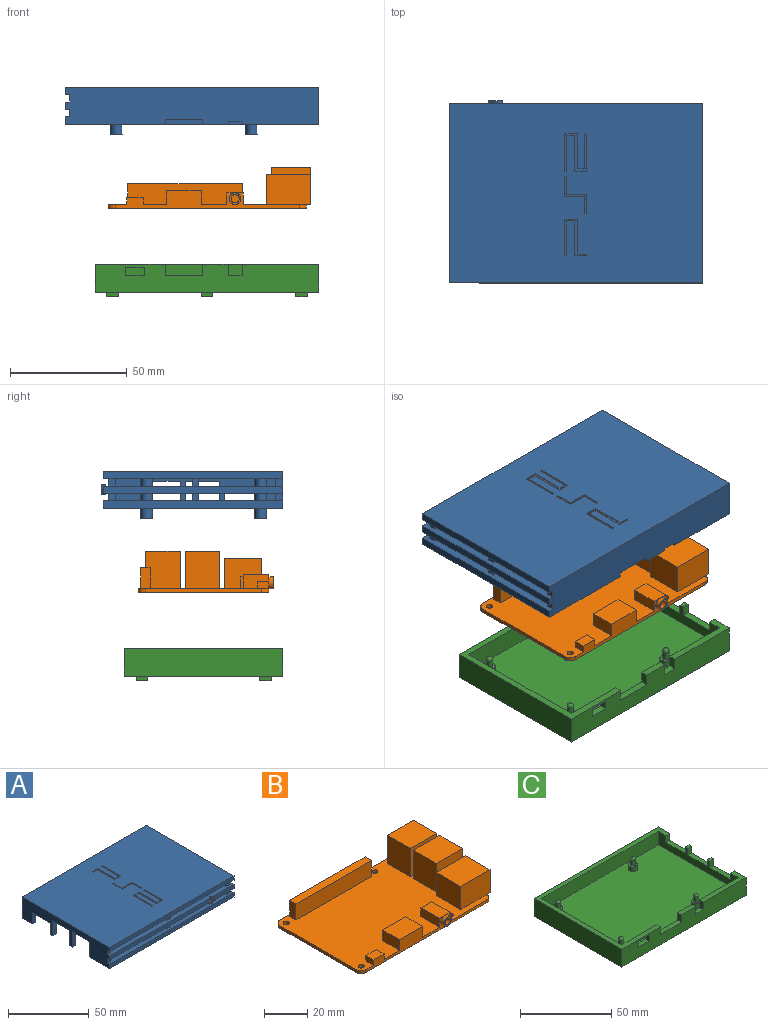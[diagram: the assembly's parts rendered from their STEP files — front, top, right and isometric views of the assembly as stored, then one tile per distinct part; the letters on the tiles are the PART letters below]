
ASSEMBLY  parts=3 mates=2
PART A: 158 faces, bbox 109x78x20.4 mm
  f0: plane 11x3mm, normal (0,0,-1), area 33mm2, adj f2,f3,f152,f156
  f1: plane 33x9mm, normal (0,0,-1), area 117mm2, adj f2,f3,f24,f27,f149,f153
  f2: plane 109x16mm, normal (0,1,0), area 1692mm2, adj f0,f1,f6,f12,f13,f24,f28,f29
  f3: plane 104x13mm, normal (0,-1,0), area 1260mm2, adj f0,f1,f6,f12,f13,f23,f25,f27
  f4: plane 3x2mm, normal (0,0,-1), area 6mm2, adj f24,f27,f146,f150
  f5: plane 3x2mm, normal (0,0,-1), area 6mm2, adj f24,f27,f144,f147
  f6: plane 109x77mm, normal (0,0,-1), area 855.6mm2, adj f2,f3,f7,f8,f9,f12,f14,f19
  f7: plane 19.8x3.21mm, normal (0,-1,0), area 58.7mm2, adj f6,f51,f65,f120,f128,f129,f130,f131
  f8: plane 3.2x3mm, normal (1,0,0), area 9.6mm2, adj f6,f21,f53,f60
  f9: plane 3.2x3mm, normal (1,0,0), area 9.6mm2, adj f6,f53,f61,f62
  f10: plane 3.2x3mm, normal (1,0,0), area 9.6mm2, adj f18,f51,f52,f58
  f11: plane 3.2x3mm, normal (1,0,0), area 9.6mm2, adj f51,f52,f59,f63
  f12: plane 3.2x3mm, normal (1,0,0), area 9.6mm2, adj f2,f3,f6,f53
  f13: plane 3.2x3mm, normal (1,0,0), area 9.6mm2, adj f2,f3,f51,f52
  f14: plane 3.2x3mm, normal (-1,0,0), area 9.6mm2, adj f6,f21,f53,f60
  f15: plane 3.2x3mm, normal (-1,0,0), area 9.6mm2, adj f18,f51,f52,f58
  f16: plane 3.2x3mm, normal (0,-1,0), area 9.6mm2, adj f24,f27,f51,f52
  f17: plane 3.2x3mm, normal (0,-1,0), area 9.6mm2, adj f48,f50,f51,f52
  f18: plane 3.2x3mm, normal (0,-1,0), area 9.6mm2, adj f10,f15,f51,f52
  f19: plane 3.2x3mm, normal (0,-1,0), area 9.6mm2, adj f6,f24,f27,f53
  f20: plane 3.2x3mm, normal (0,-1,0), area 9.6mm2, adj f6,f49,f53,f54
  f21: plane 3.2x3mm, normal (0,-1,0), area 9.6mm2, adj f6,f8,f14,f53
  f22: plane 101x10mm, normal (0,1,0), area 382.8mm2, adj f6,f23,f27,f30,f31,f48,f49,f50
  f23: plane 101x69mm, normal (0,0,-1), area 6890.5mm2, adj f3,f22,f27,f30,f32,f36,f41,f44
  f24: plane 77x16mm, normal (-1,0,0), area 733.6mm2, adj f1,f2,f4,f5,f6,f16,f19,f28
  f25: plane 62x3mm, normal (-1,0,0), area 186mm2, adj f3,f26,f28,f31
  f26: plane 90x3mm, normal (0,1,0), area 270mm2, adj f25,f27,f28,f31
  f27: plane 72x13mm, normal (1,0,0), area 409.6mm2, adj f1,f3,f4,f5,f6,f16,f19,f22
  f28: plane 109x77mm, normal (0,0,-1), area 2393.6mm2, adj f2,f3,f24,f25,f26,f27,f56,f66
  f29: plane 109x77mm, normal (0,0,1), area 8284.7mm2, adj f2,f24,f55,f64,f84,f85,f86,f87
  f30: plane 69x10mm, normal (-1,0,0), area 267.6mm2, adj f3,f6,f22,f23,f31,f51,f52,f53
  f31: plane 101x69mm, normal (0,0,1), area 1335.6mm2, adj f3,f22,f25,f26,f27,f30,f67,f68
  f32: cylinder r=2.5mm len=17.4mm, axis (0,0,1), area 273.3mm2, adj f23,f34
  f33: cylinder r=1.38mm len=17.4mm, axis (0,0,1), area 150.3mm2, adj f34,f35
  f34: plane 5x5mm, normal (0,0,-1), area 13.7mm2, adj f32,f33
  f35: plane 2.75x2.75mm, normal (0,0,-1), area 5.9mm2, adj f33
  f36: cylinder r=2.5mm len=17.4mm, axis (0,0,1), area 273.3mm2, adj f23,f38
  f37: cylinder r=1.38mm len=17.4mm, axis (0,0,1), area 150.3mm2, adj f38,f39
  f38: plane 5x5mm, normal (0,0,-1), area 13.7mm2, adj f36,f37
  f39: plane 2.75x2.75mm, normal (0,0,-1), area 5.9mm2, adj f37
  f40: cylinder r=1.38mm len=17.4mm, axis (0,0,1), area 150.3mm2, adj f42,f43
  f41: cylinder r=2.5mm len=17.4mm, axis (0,0,1), area 273.3mm2, adj f23,f42
  f42: plane 5x5mm, normal (0,0,-1), area 13.7mm2, adj f40,f41
  f43: plane 2.75x2.75mm, normal (0,0,-1), area 5.9mm2, adj f40
  f44: cylinder r=2.5mm len=17.4mm, axis (0,0,1), area 273.3mm2, adj f23,f46
  f45: cylinder r=1.38mm len=17.4mm, axis (0,0,1), area 150.3mm2, adj f46,f47
  f46: plane 5x5mm, normal (0,0,-1), area 13.7mm2, adj f44,f45
  f47: plane 2.75x2.75mm, normal (0,0,-1), area 5.9mm2, adj f45
  f48: plane 3.2x3mm, normal (-1,0,0), area 9.6mm2, adj f17,f22,f51,f52
  f49: plane 3.2x3mm, normal (1,0,0), area 9.6mm2, adj f6,f20,f22,f53
  f50: plane 3.2x3mm, normal (1,0,0), area 9.6mm2, adj f17,f22,f51,f52
  f51: plane 109x77mm, normal (0,0,1), area 858.2mm2, adj f2,f3,f7,f10,f11,f13,f15,f16
  f52: plane 109x77mm, normal (0,0,-1), area 860mm2, adj f2,f3,f10,f11,f13,f15,f16,f17
  f53: plane 109x77mm, normal (0,0,1), area 860mm2, adj f2,f3,f8,f9,f12,f14,f19,f20
  f54: plane 3.2x3mm, normal (-1,0,0), area 9.6mm2, adj f6,f20,f22,f53
  f55: plane 109x3.2mm, normal (0,-1,0), area 348.8mm2, adj f24,f29,f52,f64
  f56: plane 109x3.2mm, normal (0,-1,0), area 348.8mm2, adj f24,f28,f53,f66
  f57: plane 88.35x3.24mm, normal (0,-1,0), area 280.6mm2, adj f6,f24,f51,f119,f125
  f58: plane 3.2x3mm, normal (0,1,0), area 9.6mm2, adj f10,f15,f51,f52
  f59: plane 3.2x3mm, normal (0,-1,0), area 9.6mm2, adj f11,f30,f51,f52
  f60: plane 3.2x3mm, normal (0,1,0), area 9.6mm2, adj f6,f8,f14,f53
  f61: plane 3.2x3mm, normal (0,-1,0), area 9.6mm2, adj f6,f9,f30,f53
  f62: plane 3.2x3mm, normal (0,1,0), area 9.6mm2, adj f6,f9,f30,f53
  f63: plane 3.2x3mm, normal (0,1,0), area 9.6mm2, adj f11,f30,f51,f52
  f64: plane 77x3.2mm, normal (1,0,0), area 246.4mm2, adj f2,f29,f52,f55
  f65: plane 77x3.2mm, normal (1,0,0), area 246.4mm2, adj f2,f6,f7,f51
  f66: plane 77x3.2mm, normal (1,0,0), area 246.4mm2, adj f2,f28,f53,f56
  f67: cylinder r=1mm len=3mm, axis (0,0,-1), area 18.8mm2, adj f28,f31
  f68: cylinder r=1mm len=3mm, axis (0,0,-1), area 18.8mm2, adj f28,f31
  f69: cylinder r=1mm len=3mm, axis (0,0,-1), area 18.8mm2, adj f28,f31
  f70: cylinder r=1mm len=3mm, axis (0,0,-1), area 18.8mm2, adj f28,f31
  f71: cylinder r=1mm len=3mm, axis (0,0,-1), area 18.8mm2, adj f28,f31
  f72: cylinder r=1mm len=3mm, axis (0,0,-1), area 18.8mm2, adj f28,f31
  f73: cylinder r=1mm len=3mm, axis (0,0,-1), area 18.8mm2, adj f28,f31
  f74: cylinder r=1mm len=3mm, axis (0,0,-1), area 18.8mm2, adj f28,f31
  f75: cylinder r=1mm len=3mm, axis (0,0,-1), area 18.8mm2, adj f28,f31
  f76: cylinder r=1mm len=3mm, axis (0,0,-1), area 18.8mm2, adj f28,f31
  f77: cylinder r=1mm len=3mm, axis (0,0,-1), area 18.8mm2, adj f28,f31
  f78: cylinder r=1mm len=3mm, axis (0,0,-1), area 18.8mm2, adj f28,f31
  f79: cylinder r=1mm len=3mm, axis (0,0,-1), area 18.8mm2, adj f28,f31
  f80: cylinder r=1mm len=3mm, axis (0,0,-1), area 18.8mm2, adj f28,f31
  f81: cylinder r=1mm len=3mm, axis (0,0,-1), area 18.8mm2, adj f28,f31
  f82: cylinder r=1mm len=3mm, axis (0,0,-1), area 18.8mm2, adj f28,f31
  f83: cylinder r=1mm len=3mm, axis (0,0,-1), area 18.8mm2, adj f28,f31
  f84: plane 0.8x0.4mm, normal (0,-1,0), area 0.3mm2, adj f29,f85,f95,f96
  f85: plane 15.2x0.4mm, normal (1,0,0), area 6.1mm2, adj f29,f84,f86,f96
  f86: plane 3.4x0.4mm, normal (0,-1,0), area 1.4mm2, adj f29,f85,f87,f96
  f87: plane 15.2x0.4mm, normal (-1,0,0), area 6.1mm2, adj f29,f86,f88,f96
  f88: plane 5.1x0.4mm, normal (0,-1,0), area 2mm2, adj f29,f87,f89,f96
  f89: plane 16x0.4mm, normal (1,0,0), area 6.4mm2, adj f29,f88,f90,f96
  f90: plane 0.8x0.4mm, normal (0,1,0), area 0.3mm2, adj f29,f89,f91,f96
  f91: plane 15x0.4mm, normal (-1,0,0), area 6mm2, adj f29,f90,f92,f96
  f92: plane 3x0.4mm, normal (0,1,0), area 1.2mm2, adj f29,f91,f93,f96
  f93: plane 15x0.4mm, normal (1,0,0), area 6mm2, adj f29,f92,f94,f96
  f94: plane 5.5x0.4mm, normal (0,1,0), area 2.2mm2, adj f29,f93,f95,f96
  f95: plane 16x0.4mm, normal (-1,0,0), area 6.4mm2, adj f29,f84,f94,f96
  f96: plane 16x9.3mm, normal (0,0,1), area 52.1mm2, adj f84,f85,f86,f87,f88,f89,f90,f91
  f97: plane 8.5x0.4mm, normal (0,1,0), area 3.4mm2, adj f29,f98,f104,f105
  f98: plane 7.6x0.4mm, normal (1,0,0), area 3mm2, adj f29,f97,f99,f105
  f99: plane 0.8x0.4mm, normal (0,1,0), area 0.3mm2, adj f29,f98,f100,f105
  f100: plane 8.4x0.4mm, normal (-1,0,0), area 3.4mm2, adj f29,f99,f101,f105
  f101: plane 8.6x0.4mm, normal (0,-1,0), area 3.4mm2, adj f29,f100,f102,f105
  f102: plane 7.4x0.4mm, normal (-1,0,0), area 3mm2, adj f29,f101,f103,f105
  f103: plane 0.7x0.4mm, normal (0,-1,0), area 0.3mm2, adj f29,f102,f104,f105
  f104: plane 8.2x0.4mm, normal (1,0,0), area 3.3mm2, adj f29,f97,f103,f105
  f105: plane 15.8x9.3mm, normal (0,0,1), area 18.7mm2, adj f97,f98,f99,f100,f101,f102,f103,f104
  f106: plane 0.8x0.4mm, normal (0,-1,0), area 0.3mm2, adj f29,f107,f115,f116
  f107: plane 15x0.4mm, normal (1,0,0), area 6mm2, adj f29,f106,f108,f116
  f108: plane 3.5x0.4mm, normal (0,-1,0), area 1.4mm2, adj f29,f107,f109,f116
  f109: plane 15x0.4mm, normal (-1,0,0), area 6mm2, adj f29,f108,f110,f116
  f110: plane 5x0.4mm, normal (0,-1,0), area 2mm2, adj f29,f109,f111,f116
  f111: plane 0.8x0.4mm, normal (1,0,0), area 0.3mm2, adj f29,f110,f112,f116
  f112: plane 3.8x0.4mm, normal (0,1,0), area 1.5mm2, adj f29,f111,f113,f116
  f113: plane 15x0.4mm, normal (1,0,0), area 6mm2, adj f29,f112,f114,f116
  f114: plane 5.5x0.4mm, normal (0,1,0), area 2.2mm2, adj f29,f113,f115,f116
  f115: plane 15.8x0.4mm, normal (-1,0,0), area 6.3mm2, adj f29,f106,f114,f116
  f116: plane 15.8x9.3mm, normal (0,0,1), area 37.4mm2, adj f106,f107,f108,f109,f110,f111,f112,f113
  f117: plane 1x0.05mm, normal (0,0,1), area 0.1mm2, adj f121,f138,f139,f141
  f118: plane 1.8x0.58mm, normal (0,1,0), area 0.6mm2, adj f51,f119,f120,f137
  f119: plane 2.39x2mm, normal (-1,0,0), area 3mm2, adj f51,f57,f118,f125,f137,f139
  f120: extruded ~2.01x2mm, area 4.3mm2, adj f7,f51,f118,f135,f137,f139
  f121: plane 1x0.28mm, normal (1,0,0), area 0.3mm2, adj f117,f122,f139,f141
  f122: extruded ~1x0.02mm, area 0mm2, adj f121,f138,f139,f141
  f123: extruded ~1.27x1mm, area 2.8mm2, adj f124,f136,f139,f142
  f124: extruded ~1x0.01mm, area 0mm2, adj f123,f136,f139,f142
  f125: extruded ~2.23x2mm, area 6.7mm2, adj f6,f57,f119,f126,f139,f140
  f126: plane 2x0.28mm, normal (-1,0,0), area 0.6mm2, adj f125,f127,f139,f140
  f127: plane 2x0.85mm, normal (-0.33,0,-0.94), area 1.8mm2, adj f126,f128,f139,f140
  f128: plane 2.17x2mm, normal (0.33,0,-0.95), area 4.2mm2, adj f6,f7,f127,f129,f139,f140
  f129: extruded ~1x0.53mm, area 0.7mm2, adj f7,f128,f130,f139
  f130: plane 1x0.14mm, normal (1,0,0), area 0.1mm2, adj f7,f129,f131,f139
  f131: extruded ~2.69x1mm, area 2.9mm2, adj f7,f130,f132,f139
  f132: plane 1.89x1mm, normal (1,0,0), area 1.9mm2, adj f7,f131,f133,f139
  f133: extruded ~1x0.41mm, area 0.7mm2, adj f7,f132,f134,f139
  f134: plane 1.51x1mm, normal (-1,0,0), area 1.5mm2, adj f7,f133,f135,f139
  f135: extruded ~1.04x1mm, area 1.2mm2, adj f7,f120,f134,f139
  f136: plane 1x0.35mm, normal (-1,0,0), area 0.4mm2, adj f123,f124,f139,f142
  f137: extruded ~2x0.65mm, area 1.3mm2, adj f118,f119,f120,f139
  f138: extruded ~1.86x1mm, area 3.9mm2, adj f117,f122,f139,f141
  f139: plane 5.82x4.41mm, normal (0,-1,0), area 10.2mm2, adj f117,f119,f120,f121,f122,f123,f124,f125
  f140: plane 4.42x0.63mm, normal (0,1,0), area 1.2mm2, adj f6,f125,f126,f127,f128
  f141: plane 1.94x0.79mm, normal (0,-1,0), area 0.6mm2, adj f117,f121,f122,f138
  f142: plane 1.29x0.69mm, normal (0,-1,0), area 0.4mm2, adj f123,f124,f136
  f143: plane 15x3mm, normal (0,0,-1), area 45mm2, adj f24,f27,f144,f145
  f144: plane 11.6x3mm, normal (0,-1,0), area 34.8mm2, adj f5,f24,f27,f143
  f145: plane 11.6x3mm, normal (0,1,0), area 34.8mm2, adj f24,f27,f28,f143
  f146: plane 11.6x3mm, normal (0,-1,0), area 34.8mm2, adj f4,f24,f27,f148
  f147: plane 11.6x3mm, normal (0,1,0), area 34.8mm2, adj f5,f24,f27,f148
  f148: plane 15x3mm, normal (0,0,-1), area 45mm2, adj f24,f27,f146,f147
  f149: plane 8.6x3mm, normal (0,-1,0), area 25.8mm2, adj f1,f24,f27,f151
  f150: plane 8.6x3mm, normal (0,1,0), area 25.8mm2, adj f4,f24,f27,f151
  f151: plane 16x3mm, normal (0,0,-1), area 48mm2, adj f24,f27,f149,f150
  f152: plane 3x1.2mm, normal (-1,0,0), area 3.6mm2, adj f0,f2,f3,f154
  f153: plane 3x1.2mm, normal (1,0,0), area 3.6mm2, adj f1,f2,f3,f154
  f154: plane 6x3mm, normal (0,0,-1), area 18mm2, adj f2,f3,f152,f153
  f155: plane 3x2mm, normal (-1,0,0), area 6mm2, adj f2,f3,f28,f157
  f156: plane 3x2mm, normal (1,0,0), area 6mm2, adj f0,f2,f3,f157
  f157: plane 16x3mm, normal (0,0,-1), area 48mm2, adj f2,f3,f155,f156
PART B: 86 faces, bbox 87x58x17.6 mm
  f0: plane 16x13mm, normal (1,0,0), area 95mm2, adj f27,f28,f29,f31,f69,f70,f71,f72
  f1: plane 16x15mm, normal (1,0,0), area 156mm2, adj f17,f18,f19,f21,f59,f60,f61,f62
  f2: plane 16x15mm, normal (1,0,0), area 156mm2, adj f22,f24,f25,f26,f49,f50,f51,f52
  f3: plane 85x56mm, normal (0,0,1), area 3526.5mm2, adj f4,f5,f6,f7,f8,f9,f10,f11
  f4: plane 79x1.6mm, normal (0,1,0), area 126.4mm2, adj f3,f5,f13,f16
  f5: cylinder r=3mm len=3mm, axis (0,0,1), area 7.5mm2, adj f3,f4,f6,f16
  f6: plane 50x1.6mm, normal (-1,0,0), area 80mm2, adj f3,f5,f7,f16
  f7: cylinder r=3mm len=3mm, axis (0,0,1), area 7.5mm2, adj f3,f6,f8,f16
  f8: plane 79x7.6mm, normal (0,-1,0), area 252.8mm2, adj f3,f7,f9,f16,f32,f34,f35,f36
  f9: cylinder r=3mm len=3mm, axis (0,0,1), area 7.5mm2, adj f3,f8,f10,f16
  f10: plane 50x1.6mm, normal (1,0,0), area 80mm2, adj f3,f9,f13,f16,f17,f26,f27
  f11: cylinder r=1.38mm len=2.75mm, axis (0,0,1), area 13.8mm2, adj f3,f16
  f12: cylinder r=1.38mm len=2.75mm, axis (0,0,1), area 13.8mm2, adj f3,f16
  f13: cylinder r=3mm len=3mm, axis (0,0,1), area 7.5mm2, adj f3,f4,f10,f16
  f14: cylinder r=1.38mm len=2.75mm, axis (0,0,1), area 13.8mm2, adj f3,f16
  f15: cylinder r=1.38mm len=2.75mm, axis (0,0,1), area 13.8mm2, adj f3,f16
  f16: plane 85x56mm, normal (0,0,-1), area 4728.5mm2, adj f4,f5,f6,f7,f8,f9,f10,f11
  f17: plane 15x2mm, normal (0,0,-1), area 30mm2, adj f1,f10,f18,f19
  f18: plane 17x16mm, normal (0,-1,0), area 272mm2, adj f1,f3,f17,f20,f21
  f19: plane 17x16mm, normal (0,1,0), area 272mm2, adj f1,f3,f17,f20,f21
  f20: plane 16x15mm, normal (-1,0,0), area 240mm2, adj f3,f18,f19,f21
  f21: plane 17x15mm, normal (0,0,1), area 255mm2, adj f1,f18,f19,f20
  f22: plane 17x16mm, normal (0,1,0), area 272mm2, adj f2,f3,f23,f25,f26
  f23: plane 16x15mm, normal (-1,0,0), area 240mm2, adj f3,f22,f24,f25
  f24: plane 17x16mm, normal (0,-1,0), area 272mm2, adj f2,f3,f23,f25,f26
  f25: plane 17x15mm, normal (0,0,1), area 255mm2, adj f2,f22,f23,f24
  f26: plane 15x2mm, normal (0,0,-1), area 30mm2, adj f2,f10,f22,f24
  f27: plane 16x2mm, normal (0,0,-1), area 32mm2, adj f0,f10,f28,f29
  f28: plane 19x13mm, normal (0,-1,0), area 247mm2, adj f0,f3,f27,f30,f31
  f29: plane 19x13mm, normal (0,1,0), area 247mm2, adj f0,f3,f27,f30,f31
  f30: plane 16x13mm, normal (-1,0,0), area 208mm2, adj f3,f28,f29,f31
  f31: plane 19x16mm, normal (0,0,1), area 304mm2, adj f0,f28,f29,f30
  f32: plane 12x5mm, normal (1,0,0), area 60mm2, adj f3,f8,f33,f35
  f33: plane 7x5mm, normal (0,1,0), area 35mm2, adj f3,f32,f34,f35
  f34: plane 12x5mm, normal (-1,0,0), area 60mm2, adj f3,f8,f33,f35
  f35: plane 12x7mm, normal (0,0,1), area 84mm2, adj f8,f32,f33,f34
  f36: plane 11x6mm, normal (1,0,0), area 66mm2, adj f3,f8,f37,f39
  f37: plane 15x6mm, normal (0,1,0), area 90mm2, adj f3,f36,f38,f39
  f38: plane 11x6mm, normal (-1,0,0), area 66mm2, adj f3,f8,f37,f39
  f39: plane 15x11mm, normal (0,0,1), area 165mm2, adj f8,f36,f37,f38
  f40: plane 7x3mm, normal (0,1,0), area 21mm2, adj f3,f41,f42,f43
  f41: plane 5x3mm, normal (-1,0,0), area 15mm2, adj f3,f8,f40,f43
  f42: plane 5x3mm, normal (1,0,0), area 15mm2, adj f3,f8,f40,f43
  f43: plane 7x5mm, normal (0,0,1), area 35mm2, adj f8,f40,f41,f42
  f44: plane 49x9mm, normal (0,1,0), area 441mm2, adj f3,f45,f47,f48
  f45: plane 9x4mm, normal (-1,0,0), area 36mm2, adj f3,f44,f46,f48
  f46: plane 49x9mm, normal (0,-1,0), area 441mm2, adj f3,f45,f47,f48
  f47: plane 9x4mm, normal (1,0,0), area 36mm2, adj f3,f44,f46,f48
  f48: plane 49x4mm, normal (0,0,1), area 196mm2, adj f44,f45,f46,f47
  f49: plane 9x3.5mm, normal (0,-1,0), area 31.5mm2, adj f2,f50,f52,f53
  f50: plane 12x9mm, normal (0,0,-1), area 108mm2, adj f2,f49,f51,f53
  f51: plane 9x3.5mm, normal (0,1,0), area 31.5mm2, adj f2,f50,f52,f53
  f52: plane 12x9mm, normal (0,0,1), area 108mm2, adj f2,f49,f51,f53
  f53: plane 12x3.5mm, normal (1,0,0), area 42mm2, adj f49,f50,f51,f52
  f54: plane 12x9mm, normal (0,0,-1), area 108mm2, adj f2,f55,f57,f58
  f55: plane 9x3.5mm, normal (0,1,0), area 31.5mm2, adj f2,f54,f56,f58
  f56: plane 12x9mm, normal (0,0,1), area 108mm2, adj f2,f55,f57,f58
  f57: plane 9x3.5mm, normal (0,-1,0), area 31.5mm2, adj f2,f54,f56,f58
  f58: plane 12x3.5mm, normal (1,0,0), area 42mm2, adj f54,f55,f56,f57
  f59: plane 9x3.5mm, normal (0,-1,0), area 31.5mm2, adj f1,f60,f62,f63
  f60: plane 12x9mm, normal (0,0,-1), area 108mm2, adj f1,f59,f61,f63
  f61: plane 9x3.5mm, normal (0,1,0), area 31.5mm2, adj f1,f60,f62,f63
  f62: plane 12x9mm, normal (0,0,1), area 108mm2, adj f1,f59,f61,f63
  f63: plane 12x3.5mm, normal (1,0,0), area 42mm2, adj f59,f60,f61,f62
  f64: plane 12x9mm, normal (0,0,-1), area 108mm2, adj f1,f65,f67,f68
  f65: plane 9x3.5mm, normal (0,1,0), area 31.5mm2, adj f1,f64,f66,f68
  f66: plane 12x9mm, normal (0,0,1), area 108mm2, adj f1,f65,f67,f68
  f67: plane 9x3.5mm, normal (0,-1,0), area 31.5mm2, adj f1,f64,f66,f68
  f68: plane 12x3.5mm, normal (1,0,0), area 42mm2, adj f64,f65,f66,f67
  f69: plane 14x10.5mm, normal (0,0,-1), area 147mm2, adj f0,f70,f80,f81
  f70: plane 10.5x7mm, normal (0,1,0), area 73.5mm2, adj f0,f69,f71,f81
  f71: plane 10.5x4mm, normal (0,0,1), area 42mm2, adj f0,f70,f72,f81
  f72: plane 10.5x2mm, normal (0,1,0), area 21mm2, adj f0,f71,f73,f81
  f73: plane 10.5x1.5mm, normal (0,0,1), area 15.8mm2, adj f0,f72,f74,f81
  f74: plane 10.5x1mm, normal (0,1,0), area 10.5mm2, adj f0,f73,f75,f81
  f75: plane 10.5x3mm, normal (0,0,1), area 31.5mm2, adj f0,f74,f76,f81
  f76: plane 10.5x1mm, normal (0,-1,0), area 10.5mm2, adj f0,f75,f77,f81
  f77: plane 10.5x1.5mm, normal (0,0,1), area 15.7mm2, adj f0,f76,f78,f81
  f78: plane 10.5x2mm, normal (0,-1,0), area 21mm2, adj f0,f77,f79,f81
  f79: plane 10.5x4mm, normal (0,0,1), area 42mm2, adj f0,f78,f80,f81
  f80: plane 10.5x7mm, normal (0,-1,0), area 73.5mm2, adj f0,f69,f79,f81
  f81: plane 14x10mm, normal (1,0,0), area 113mm2, adj f69,f70,f71,f72,f73,f74,f75,f76
  f82: cylinder r=2.5mm len=5mm, axis (0,1,0), area 31.4mm2, adj f8,f83
  f83: plane 5x5mm, normal (0,-1,0), area 10mm2, adj f82,f84
  f84: cylinder r=1.75mm len=5mm, axis (0,-1,0), area 55mm2, adj f83,f85
  f85: plane 3.5x3.5mm, normal (0,-1,0), area 9.6mm2, adj f84
PART C: 80 faces, bbox 96x68x14 mm
  f0: plane 33x9mm, normal (0,0,1), area 117mm2, adj f2,f3,f8,f9,f37,f77
  f1: plane 11x3mm, normal (0,0,1), area 33mm2, adj f2,f3,f75,f78
  f2: plane 96x12mm, normal (0,-1,0), area 1011.6mm2, adj f0,f1,f4,f7,f8,f12,f70,f71
  f3: plane 90x9mm, normal (0,1,0), area 669.6mm2, adj f0,f1,f7,f9,f10,f13,f70,f71
  f4: plane 96x68mm, normal (0,0,-1), area 6378mm2, adj f2,f8,f11,f12,f40,f41,f42,f43
  f5: plane 3x2mm, normal (0,0,1), area 6mm2, adj f8,f9,f34,f39
  f6: plane 3x2mm, normal (0,0,1), area 6mm2, adj f8,f9,f31,f36
  f7: plane 96x68mm, normal (0,0,1), area 582mm2, adj f2,f3,f8,f9,f11,f12,f13,f14
  f8: plane 68x12mm, normal (1,0,0), area 613.6mm2, adj f0,f2,f4,f5,f6,f7,f11,f31
  f9: plane 62x9mm, normal (-1,0,0), area 355.6mm2, adj f0,f3,f5,f6,f7,f10,f14,f31
  f10: plane 90x62mm, normal (0,0,1), area 5501.5mm2, adj f3,f9,f13,f14,f15,f19,f23,f27
  f11: plane 96x12mm, normal (0,1,0), area 1152mm2, adj f4,f7,f8,f12
  f12: plane 68x12mm, normal (-1,0,0), area 816mm2, adj f2,f4,f7,f11
  f13: plane 62x9mm, normal (1,0,0), area 558mm2, adj f3,f7,f10,f14
  f14: plane 90x9mm, normal (0,-1,0), area 810mm2, adj f7,f9,f10,f13
  f15: cylinder r=2.5mm len=5mm, axis (0,0,-1), area 47.1mm2, adj f10,f16
  f16: plane 5x5mm, normal (0,0,1), area 13.7mm2, adj f15,f18
  f17: sphere r=1.38mm, area 11.9mm2, adj f18
  f18: cylinder r=1.38mm len=3.63mm, axis (0,0,-1), area 31.3mm2, adj f16,f17
  f19: cylinder r=2.5mm len=5mm, axis (0,0,-1), area 47.1mm2, adj f10,f20
  f20: plane 5x5mm, normal (0,0,1), area 13.7mm2, adj f19,f22
  f21: sphere r=1.38mm, area 11.9mm2, adj f22
  f22: cylinder r=1.38mm len=3.63mm, axis (0,0,-1), area 31.3mm2, adj f20,f21
  f23: cylinder r=2.5mm len=5mm, axis (0,0,-1), area 47.1mm2, adj f10,f24
  f24: plane 5x5mm, normal (0,0,1), area 13.7mm2, adj f23,f26
  f25: sphere r=1.38mm, area 11.9mm2, adj f26
  f26: cylinder r=1.38mm len=3.63mm, axis (0,0,-1), area 31.3mm2, adj f24,f25
  f27: cylinder r=2.5mm len=5mm, axis (0,0,-1), area 47.1mm2, adj f10,f28
  f28: plane 5x5mm, normal (0,0,1), area 13.7mm2, adj f27,f30
  f29: sphere r=1.38mm, area 11.9mm2, adj f30
  f30: cylinder r=1.38mm len=3.63mm, axis (0,0,-1), area 31.3mm2, adj f28,f29
  f31: plane 4.4x3mm, normal (0,1,0), area 13.2mm2, adj f6,f8,f9,f32
  f32: plane 15x3mm, normal (0,0,1), area 45mm2, adj f8,f9,f31,f33
  f33: plane 4.4x3mm, normal (0,-1,0), area 13.2mm2, adj f7,f8,f9,f32
  f34: plane 4.4x3mm, normal (0,1,0), area 13.2mm2, adj f5,f8,f9,f35
  f35: plane 15x3mm, normal (0,0,1), area 45mm2, adj f8,f9,f34,f36
  f36: plane 4.4x3mm, normal (0,-1,0), area 13.2mm2, adj f6,f8,f9,f35
  f37: plane 4.4x3mm, normal (0,1,0), area 13.2mm2, adj f0,f8,f9,f38
  f38: plane 16x3mm, normal (0,0,1), area 48mm2, adj f8,f9,f37,f39
  f39: plane 4.4x3mm, normal (0,-1,0), area 13.2mm2, adj f5,f8,f9,f38
  f40: plane 5x2mm, normal (0,-1,0), area 10mm2, adj f4,f41,f43,f44
  f41: plane 5x2mm, normal (-1,0,0), area 10mm2, adj f4,f40,f42,f44
  f42: plane 5x2mm, normal (0,1,0), area 10mm2, adj f4,f41,f43,f44
  f43: plane 5x2mm, normal (1,0,0), area 10mm2, adj f4,f40,f42,f44
  f44: plane 5x5mm, normal (0,0,-1), area 25mm2, adj f40,f41,f42,f43
  f45: plane 5x2mm, normal (0,-1,0), area 10mm2, adj f4,f46,f48,f49
  f46: plane 5x2mm, normal (-1,0,0), area 10mm2, adj f4,f45,f47,f49
  f47: plane 5x2mm, normal (0,1,0), area 10mm2, adj f4,f46,f48,f49
  f48: plane 5x2mm, normal (1,0,0), area 10mm2, adj f4,f45,f47,f49
  f49: plane 5x5mm, normal (0,0,-1), area 25mm2, adj f45,f46,f47,f48
  f50: plane 5x2mm, normal (1,0,0), area 10mm2, adj f4,f51,f53,f54
  f51: plane 5x2mm, normal (0,-1,0), area 10mm2, adj f4,f50,f52,f54
  f52: plane 5x2mm, normal (-1,0,0), area 10mm2, adj f4,f51,f53,f54
  f53: plane 5x2mm, normal (0,1,0), area 10mm2, adj f4,f50,f52,f54
  f54: plane 5x5mm, normal (0,0,-1), area 25mm2, adj f50,f51,f52,f53
  f55: plane 5x2mm, normal (0,1,0), area 10mm2, adj f4,f56,f58,f59
  f56: plane 5x2mm, normal (1,0,0), area 10mm2, adj f4,f55,f57,f59
  f57: plane 5x2mm, normal (0,-1,0), area 10mm2, adj f4,f56,f58,f59
  f58: plane 5x2mm, normal (-1,0,0), area 10mm2, adj f4,f55,f57,f59
  f59: plane 5x5mm, normal (0,0,-1), area 25mm2, adj f55,f56,f57,f58
  f60: plane 5x2mm, normal (1,0,0), area 10mm2, adj f4,f61,f63,f64
  f61: plane 5x2mm, normal (0,-1,0), area 10mm2, adj f4,f60,f62,f64
  f62: plane 5x2mm, normal (-1,0,0), area 10mm2, adj f4,f61,f63,f64
  f63: plane 5x2mm, normal (0,1,0), area 10mm2, adj f4,f60,f62,f64
  f64: plane 5x5mm, normal (0,0,-1), area 25mm2, adj f60,f61,f62,f63
  f65: plane 5x2mm, normal (0,1,0), area 10mm2, adj f4,f66,f68,f69
  f66: plane 5x2mm, normal (1,0,0), area 10mm2, adj f4,f65,f67,f69
  f67: plane 5x2mm, normal (0,-1,0), area 10mm2, adj f4,f66,f68,f69
  f68: plane 5x2mm, normal (-1,0,0), area 10mm2, adj f4,f65,f67,f69
  f69: plane 5x5mm, normal (0,0,-1), area 25mm2, adj f65,f66,f67,f68
  f70: plane 8x3mm, normal (0,0,1), area 24mm2, adj f2,f3,f71,f73
  f71: plane 3.8x3mm, normal (-1,0,0), area 11.4mm2, adj f2,f3,f70,f72
  f72: plane 8x3mm, normal (0,0,-1), area 24mm2, adj f2,f3,f71,f73
  f73: plane 3.8x3mm, normal (1,0,0), area 11.4mm2, adj f2,f3,f70,f72
  f74: plane 16x3mm, normal (0,0,1), area 48mm2, adj f2,f3,f75,f76
  f75: plane 5x3mm, normal (-1,0,0), area 15mm2, adj f1,f2,f3,f74
  f76: plane 5x3mm, normal (1,0,0), area 15mm2, adj f2,f3,f7,f74
  f77: plane 5x3mm, normal (-1,0,0), area 15mm2, adj f0,f2,f3,f79
  f78: plane 5x3mm, normal (1,0,0), area 15mm2, adj f1,f2,f3,f79
  f79: plane 6x3mm, normal (0,0,1), area 18mm2, adj f2,f3,f77,f78
PLACE A rot(axis=(0,0,1),180deg) t=(-80.96,-65.91,76.16)mm
PLACE B t=(-80.96,-65.91,28.76)mm
PLACE C t=(-80.96,-65.91,-5.84)mm
MATE planar A.f36 <-> B.f11  axis (0,0,-1) through (-119.96,-41.41,58.76)mm
MATE planar C.f27 <-> B.f15  axis (0,0,1) through (-61.96,-90.41,-2.84)mm
